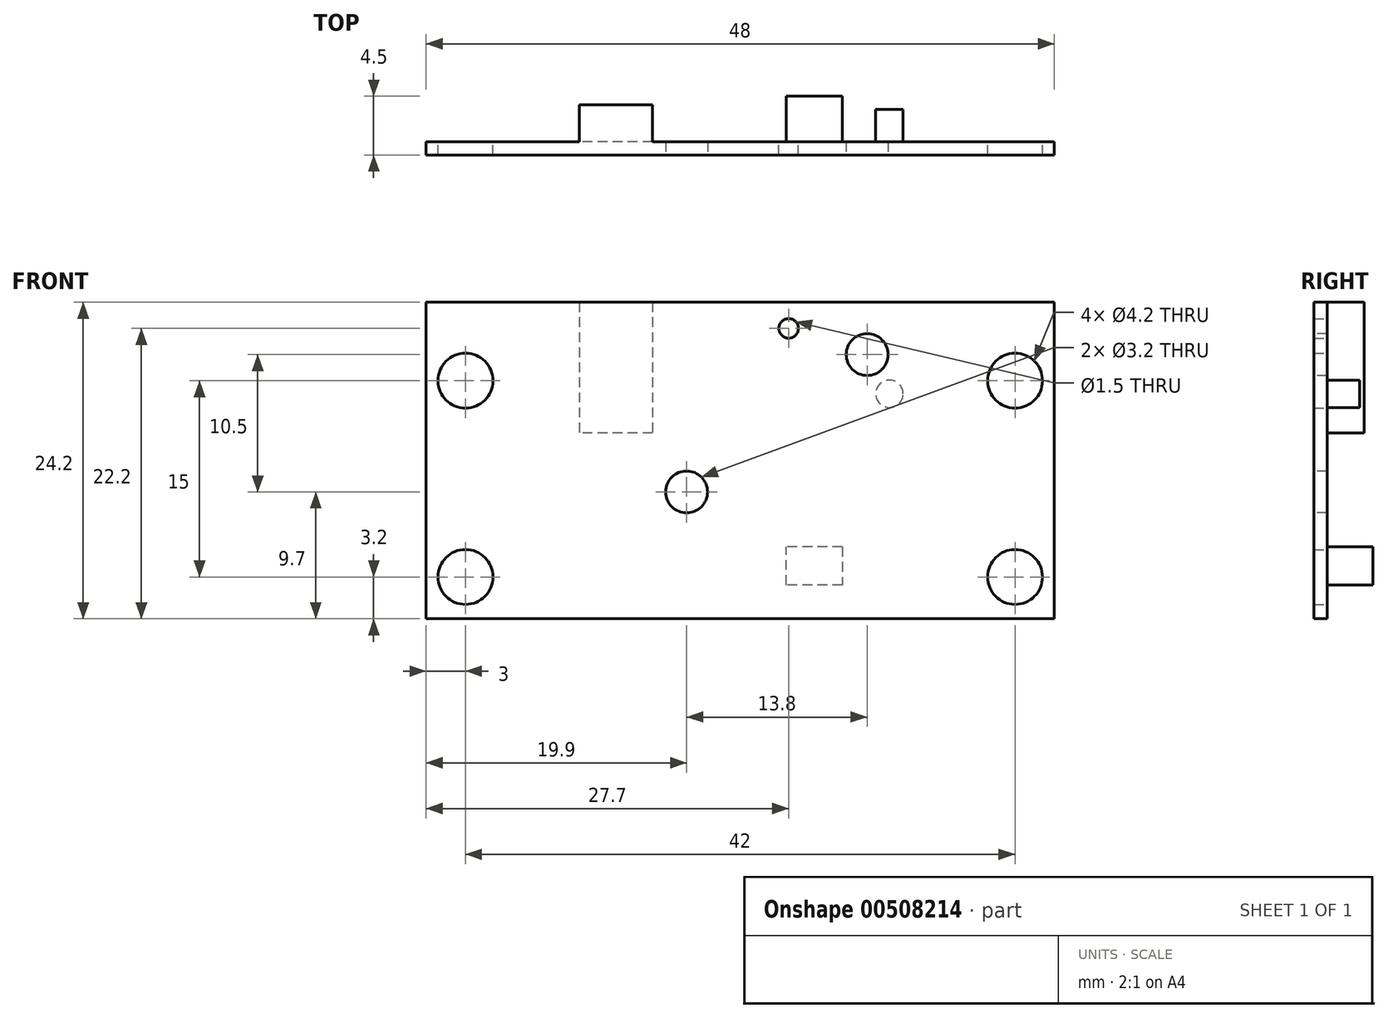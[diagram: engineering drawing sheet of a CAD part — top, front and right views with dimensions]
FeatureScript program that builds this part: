
annotation { "Feature Type Name" : "Feature", "Feature Type Description" : "" }
export const myFeature = defineFeature(function(context is Context, id is Id, definition is map)
    precondition{}
    {
        {
            var Q0;
            Q0=qCreatedBy(makeId("Front.planeOp"),FACE);
            var sketch = newSketch(context, id + "F0", { "sketchPlane" : qUnion([Q0])});
            skLineSegment(sketch, "E0.bottom", {"start": v(24, -12.1) * mm, "end": v(-24, -12.1) * mm});
            skLineSegment(sketch, "E0.top", {"start": v(24, 12.1) * mm, "end": v(-24, 12.1) * mm});
            skLineSegment(sketch, "E0.left", {"start": v(24, -12.1) * mm, "end": v(24, 12.1) * mm});
            skLineSegment(sketch, "E0.right", {"start": v(-24, -12.1) * mm, "end": v(-24, 12.1) * mm});
            skPoint(sketch, "E0.middle", {"position": v(0, 0) * mm});
            skCircle(sketch, "E1", {"center": v(9.7, 8.1) * mm, "radius": 1.6 * mm});
            skCircle(sketch, "E2", {"center": v(-4.1, -2.4) * mm, "radius": 1.6 * mm});
            skSolve(sketch);
        }
        {
            var Q0;
            {var subQ0=sQuery(id+"F0.wireOp",EDGE,"E0.right");Q0=makeQuery(id+"F0.imprint","IMPRINT",FACE,{"disambiguationData":[TD([[makeQuery(id+"F0.imprint","IMPRINT",EDGE,{"derivedFrom":subQ0}),-1.0]])]});}
            var Q1;
            Q1=makeQuery(id+"F0.imprint","IMPRINT",FACE,{"disambiguationData":[TD([[makeQuery(id+"F0.imprint","IMPRINT",EDGE,{"derivedFrom":sQuery(id+"F0.wireOp",EDGE,"E1")}),-1.0]])]});
            var Q2;
            {var subQ4=sQuery(id+"F0.wireOp",EDGE,"E0.left");Q2=makeQuery(id+"F0.imprint","IMPRINT",FACE,{"disambiguationData":[TD([[makeQuery(id+"F0.imprint","IMPRINT",EDGE,{"derivedFrom":subQ4}),1.0]])]});}
            extrude(context, id + "F1", {"entities" : qUnion([Q0, Q1, Q2]), "oppositeDirection" : true, "depth" : 1 * mm, "offsetDistance" : 25 * mm});
        }
        {
            var Q0;
            Q0=makeQuery(id+"F1.opExtrude","CAP_FACE",FACE,{"disambiguationData":[OSD([sQuery(id+"F0.wireOp",EDGE,"E0.bottom"),sQuery(id+"F0.wireOp",EDGE,"E0.top"),sQuery(id+"F0.wireOp",EDGE,"E0.left"),sQuery(id+"F0.wireOp",EDGE,"E0.right"),sQuery(id+"F0.wireOp",EDGE,"E1"),sQuery(id+"F0.wireOp",EDGE,"E2"),sQuery(id+"F0.wireOp",EDGE,"masoxanN-hD2c-xeoc-2SMM-YdOjzVfdmSgA")])],"isStart":false});
            var sketch = newSketch(context, id + "F2", { "sketchPlane" : qUnion([Q0])});
            skLineSegment(sketch, "E3", {"start": v(-7.8, -6.6) * mm, "end": v(-7.8, -9.5) * mm});
            skLineSegment(sketch, "E4", {"start": v(-7.8, -9.5) * mm, "end": v(-3.5, -9.5) * mm});
            skLineSegment(sketch, "E5", {"start": v(-3.5, -9.5) * mm, "end": v(-3.5, -6.6) * mm});
            skCircle(sketch, "E6.0", {"center": v(4.1, -2.4) * mm, "radius": 1.6 * mm});
            skCircle(sketch, "E7.0", {"center": v(-9.7, 8.1) * mm, "radius": 1.6 * mm, "construction": true});
            skCircle(sketch, "E8", {"center": v(-3.7, 10.1) * mm, "radius": 0.75 * mm});
            skCircle(sketch, "E9", {"center": v(-11.4, 5.1) * mm, "radius": 1.05 * mm});
            skLineSegment(sketch, "E10", {"start": v(-7.8, -6.6) * mm, "end": v(-3.5, -6.6) * mm});
            skCircle(sketch, "E11", {"center": v(-21, 6.1) * mm, "radius": 2.1 * mm});
            skCircle(sketch, "E12", {"center": v(-21, -8.9) * mm, "radius": 2.1 * mm});
            skCircle(sketch, "E13", {"center": v(21, 6.1) * mm, "radius": 2.1 * mm});
            skCircle(sketch, "E14", {"center": v(21, -8.9) * mm, "radius": 2.1 * mm});
            skSolve(sketch);
        }
        {
            var Q0;
            Q0=makeQuery(id+"F2.imprint","IMPRINT",FACE,{"disambiguationData":[TD([[makeQuery(id+"F2.imprint","IMPRINT",EDGE,{"derivedFrom":sQuery(id+"F2.wireOp",EDGE,"E9")}),1.0]])]});
            extrude(context, id + "F3", {"entities" : qUnion([Q0]), "operationType" : NewBodyOperationType.ADD, "depth" : 2.5 * mm, "offsetDistance" : 25 * mm});
        }
        {
            var Q0;
            Q0=makeQuery(id+"F2.imprint","IMPRINT",FACE,{"disambiguationData":[TD([[makeQuery(id+"F2.imprint","IMPRINT",EDGE,{"derivedFrom":sQuery(id+"F2.wireOp",EDGE,"E11")}),1.0]])]});
            var Q1;
            Q1=makeQuery(id+"F2.imprint","IMPRINT",FACE,{"disambiguationData":[TD([[makeQuery(id+"F2.imprint","IMPRINT",EDGE,{"derivedFrom":sQuery(id+"F2.wireOp",EDGE,"E12")}),1.0]])]});
            var Q2;
            Q2=makeQuery(id+"F2.imprint","IMPRINT",FACE,{"disambiguationData":[TD([[makeQuery(id+"F2.imprint","IMPRINT",EDGE,{"derivedFrom":sQuery(id+"F2.wireOp",EDGE,"E13")}),1.0]])]});
            var Q3;
            Q3=makeQuery(id+"F2.imprint","IMPRINT",FACE,{"disambiguationData":[TD([[makeQuery(id+"F2.imprint","IMPRINT",EDGE,{"derivedFrom":sQuery(id+"F2.wireOp",EDGE,"E14")}),1.0]])]});
            var Q4;
            Q4=makeQuery(id+"F2.imprint","IMPRINT",FACE,{"disambiguationData":[TD([[makeQuery(id+"F2.imprint","IMPRINT",EDGE,{"derivedFrom":sQuery(id+"F2.wireOp",EDGE,"E8")}),1.0]])]});
            extrude(context, id + "F4", {"entities" : qUnion([Q0, Q1, Q2, Q3, Q4]), "operationType" : NewBodyOperationType.REMOVE, "endBound" : BoundingType.THROUGH_ALL, "oppositeDirection" : true, "depth" : 25 * mm, "offsetDistance" : 25 * mm});
        }
        {
            var Q0;
            Q0=makeQuery(id+"F2.imprint","IMPRINT",FACE,{"disambiguationData":[TD([[makeQuery(id+"F2.imprint","IMPRINT",EDGE,{"derivedFrom":sQuery(id+"F2.wireOp",EDGE,"E3")}),-1.0]])]});
            var sketch = newSketch(context, id + "F5", { "sketchPlane" : qUnion([Q0])});
            skLineSegment(sketch, "E15", {"start": v(6.7, 2.1) * mm, "end": v(12.3, 2.1) * mm});
            skLineSegment(sketch, "E16", {"start": v(12.3, 12.1) * mm, "end": v(6.7, 12.1) * mm});
            skLineSegment(sketch, "E17", {"start": v(6.7, 12.1) * mm, "end": v(6.7, 2.1) * mm});
            skLineSegment(sketch, "E18", {"start": v(12.3, 12.1) * mm, "end": v(12.3, 2.1) * mm});
            skSolve(sketch);
        }
        {
            var Q0;
            Q0=makeQuery(id+"F5.imprint","IMPRINT",FACE,{"disambiguationData":[TD([[makeQuery(id+"F5.imprint","IMPRINT",EDGE,{"derivedFrom":sQuery(id+"F5.wireOp",EDGE,"E15")}),1.0]])]});
            extrude(context, id + "F6", {"entities" : qUnion([Q0]), "operationType" : NewBodyOperationType.ADD, "depth" : 2.85 * mm, "offsetDistance" : 25 * mm});
        }
        {
            var Q0;
            Q0=makeQuery(id+"F2.imprint","IMPRINT",FACE,{"disambiguationData":[TD([[makeQuery(id+"F2.imprint","IMPRINT",EDGE,{"derivedFrom":sQuery(id+"F2.wireOp",EDGE,"E3")}),1.0]])]});
            extrude(context, id + "F7", {"entities" : qUnion([Q0]), "operationType" : NewBodyOperationType.ADD, "depth" : 3.5 * mm, "offsetDistance" : 25 * mm});
        }
    });
